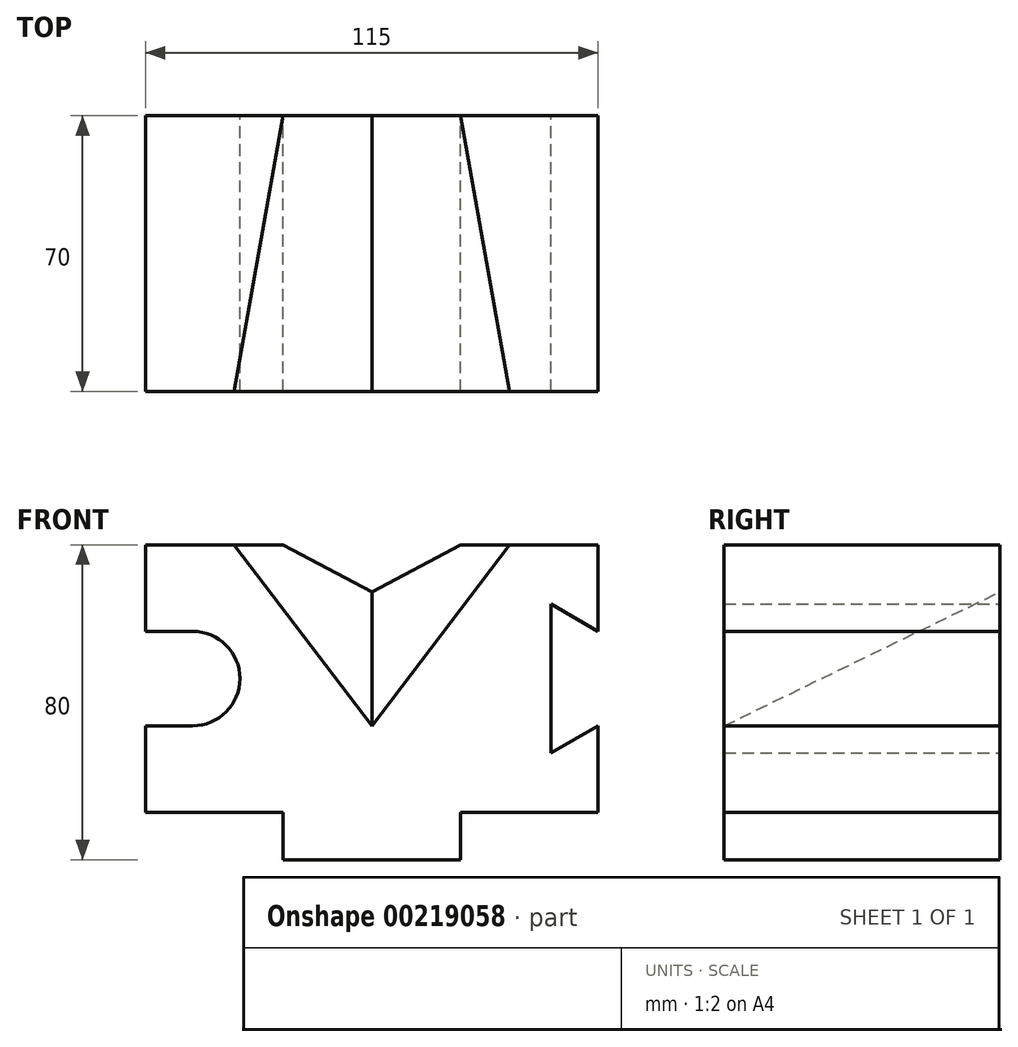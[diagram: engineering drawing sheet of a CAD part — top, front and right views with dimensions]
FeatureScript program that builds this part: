
annotation { "Feature Type Name" : "Feature", "Feature Type Description" : "" }
export const myFeature = defineFeature(function(context is Context, id is Id, definition is map)
    precondition{}
    {
        {
            var Q0;
            Q0=qCreatedBy(makeId("Front.planeOp"),FACE);
            var sketch = newSketch(context, id + "F0", { "sketchPlane" : qUnion([Q0])});
            skLineSegment(sketch, "E0", {"start": v(0, 12) * mm, "end": v(35, 12) * mm});
            skLineSegment(sketch, "E1", {"start": v(35, 12) * mm, "end": v(35, 0) * mm});
            skLineSegment(sketch, "E2", {"start": v(35, 0) * mm, "end": v(80, 0) * mm});
            skLineSegment(sketch, "E3", {"start": v(80, 0) * mm, "end": v(80, 12) * mm});
            skLineSegment(sketch, "E4", {"start": v(80, 12) * mm, "end": v(115, 12) * mm});
            skLineSegment(sketch, "E5", {"start": v(115, 12) * mm, "end": v(115, 34) * mm});
            skLineSegment(sketch, "E6", {"start": v(115, 80) * mm, "end": v(115, 58) * mm});
            skLineSegment(sketch, "E7", {"start": v(80, 80) * mm, "end": v(80, 80) * mm});
            skPoint(sketch, "E8.endSnap0", {"position": v(57.5, 0) * mm});
            skLineSegment(sketch, "E9", {"start": v(0, 80) * mm, "end": v(0, 58) * mm});
            skLineSegment(sketch, "E10", {"start": v(0, 58) * mm, "end": v(12, 58) * mm});
            skLineSegment(sketch, "E11", {"start": v(0, 34) * mm, "end": v(12, 34) * mm});
            skLineSegment(sketch, "E12", {"start": v(115, 58) * mm, "end": v(103, 64.93) * mm});
            skLineSegment(sketch, "E13", {"start": v(103, 64.93) * mm, "end": v(103, 27.07) * mm});
            skLineSegment(sketch, "E14", {"start": v(103, 27.07) * mm, "end": v(115, 34) * mm});
            skLineSegment(sketch, "E15.trimOffspring", {"start": v(0, 38.58) * mm, "end": v(0, 12) * mm});
            skPoint(sketch, "E16.center.orphan", {"position": v(12, 52) * mm});
            skArc(sketch, "E17", {"start": v(12, 34) * mm, "mid": v(24, 46) * mm, "end": v(12, 58) * mm});
            skLineSegment(sketch, "E18", {"start": v(0, 80) * mm, "end": v(115, 80) * mm});
            skSolve(sketch);
        }
        {
            var Q0;
            Q0 = qSketchRegion(id + "F0", true);
            extrude(context, id + "F1", {"entities" : qUnion([Q0]), "depth" : 70 * mm});
        }
        {
            var Q0;
            Q0=makeQuery(id+"F1.opExtrude","CAP_FACE",FACE,{"disambiguationData":[OSD([sQuery(id+"F0.wireOp",EDGE,"E0"),sQuery(id+"F0.wireOp",EDGE,"E1"),sQuery(id+"F0.wireOp",EDGE,"E2"),sQuery(id+"F0.wireOp",EDGE,"E3"),sQuery(id+"F0.wireOp",EDGE,"E4"),sQuery(id+"F0.wireOp",EDGE,"E5"),sQuery(id+"F0.wireOp",EDGE,"E6"),sQuery(id+"F0.wireOp",EDGE,"Aqdttwug-7BTY-vIay-fNMC-P576xLi7TuAD"),sQuery(id+"F0.wireOp",EDGE,"E8"),sQuery(id+"F0.wireOp",EDGE,"YIk0LJDN-VCy3-c42S-syPJ-LJre9iLl8tl2"),sQuery(id+"F0.wireOp",EDGE,"3mUWEbxa-kyO5-99bo-JKzv-BWnynAJJwmwq"),sQuery(id+"F0.wireOp",EDGE,"qfJHtdMm-ixyH-VtD0-88eF-w4xuVrCJPXzm"),sQuery(id+"F0.wireOp",EDGE,"E9"),sQuery(id+"F0.wireOp",EDGE,"E10"),sQuery(id+"F0.wireOp",EDGE,"E11"),sQuery(id+"F0.wireOp",EDGE,"E12"),sQuery(id+"F0.wireOp",EDGE,"E13"),sQuery(id+"F0.wireOp",EDGE,"E14"),sQuery(id+"F0.wireOp",EDGE,"E15.trimOffspring"),sQuery(id+"F0.wireOp",EDGE,"E17")])],"isStart":true});
            var sketch = newSketch(context, id + "F2", { "sketchPlane" : qUnion([Q0])});
            skLineSegment(sketch, "E19.0", {"start": v(-57.5, 68) * mm, "end": v(-35, 80) * mm});
            skLineSegment(sketch, "E20.0", {"start": v(-80, 80) * mm, "end": v(-57.5, 68) * mm});
            skLineSegment(sketch, "E21", {"start": v(-35, 80) * mm, "end": v(-80, 80) * mm});
            skSolve(sketch);
        }
        {
            var Q0;
            Q0=makeQuery(id+"F1.opExtrude","CAP_FACE",FACE,{"disambiguationData":[OSD([sQuery(id+"F0.wireOp",EDGE,"E0"),sQuery(id+"F0.wireOp",EDGE,"E1"),sQuery(id+"F0.wireOp",EDGE,"E2"),sQuery(id+"F0.wireOp",EDGE,"E3"),sQuery(id+"F0.wireOp",EDGE,"E4"),sQuery(id+"F0.wireOp",EDGE,"E5"),sQuery(id+"F0.wireOp",EDGE,"E6"),sQuery(id+"F0.wireOp",EDGE,"Aqdttwug-7BTY-vIay-fNMC-P576xLi7TuAD"),sQuery(id+"F0.wireOp",EDGE,"E8"),sQuery(id+"F0.wireOp",EDGE,"YIk0LJDN-VCy3-c42S-syPJ-LJre9iLl8tl2"),sQuery(id+"F0.wireOp",EDGE,"3mUWEbxa-kyO5-99bo-JKzv-BWnynAJJwmwq"),sQuery(id+"F0.wireOp",EDGE,"qfJHtdMm-ixyH-VtD0-88eF-w4xuVrCJPXzm"),sQuery(id+"F0.wireOp",EDGE,"E9"),sQuery(id+"F0.wireOp",EDGE,"E10"),sQuery(id+"F0.wireOp",EDGE,"E11"),sQuery(id+"F0.wireOp",EDGE,"E12"),sQuery(id+"F0.wireOp",EDGE,"E13"),sQuery(id+"F0.wireOp",EDGE,"E14"),sQuery(id+"F0.wireOp",EDGE,"E15.trimOffspring"),sQuery(id+"F0.wireOp",EDGE,"E17")])],"isStart":false});
            var sketch = newSketch(context, id + "F3", { "sketchPlane" : qUnion([Q0])});
            skLineSegment(sketch, "E22", {"start": v(22.5, 80) * mm, "end": v(57.5, 34) * mm});
            skLineSegment(sketch, "E23", {"start": v(57.5, 34) * mm, "end": v(92.5, 80) * mm});
            skLineSegment(sketch, "E24", {"start": v(92.5, 80) * mm, "end": v(22.5, 80) * mm});
            skSolve(sketch);
        }
        {
            var Q1;
            Q1 = qSketchRegion(id + "F3", true);
            var Q2;
            Q2 = qSketchRegion(id + "F2", true);
            loft(context, id + "F4", {"operationType" : NewBodyOperationType.REMOVE, "sheetProfilesArray" : [{ "sheetProfileEntities" : qUnion([Q1]) }, { "sheetProfileEntities" : qUnion([Q2]) }]});
        }
    });
